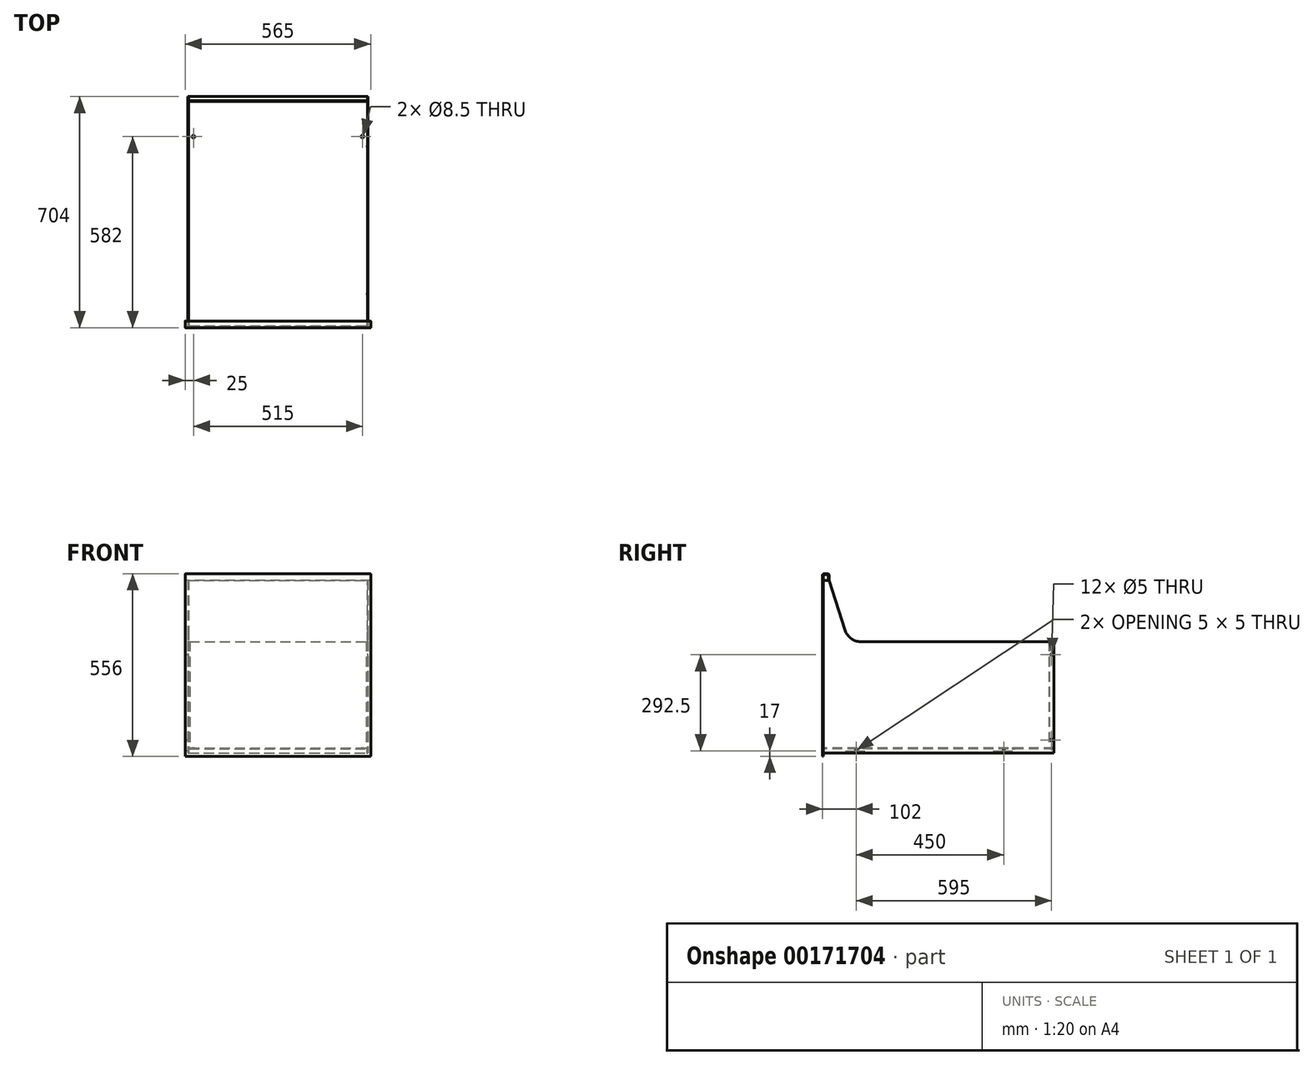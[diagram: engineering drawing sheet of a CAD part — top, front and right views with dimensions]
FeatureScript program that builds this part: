
annotation { "Feature Type Name" : "Feature", "Feature Type Description" : "" }
export const myFeature = defineFeature(function(context is Context, id is Id, definition is map)
    precondition{}
    {
        {
            var Q0;
            Q0=qCreatedBy(makeId("Top.planeOp"),FACE);
            var sketch = newSketch(context, id + "F0", { "sketchPlane" : qUnion([Q0])});
            skLineSegment(sketch, "E0.top", {"start": v(-270.5, -351) * mm, "end": v(270.5, -351) * mm});
            skLineSegment(sketch, "E0.left", {"start": v(-274.5, 351) * mm, "end": v(-274.5, -347) * mm});
            skLineSegment(sketch, "E0.right", {"start": v(274.5, 351) * mm, "end": v(274.5, -347) * mm});
            skPoint(sketch, "E0.middle", {"position": v(0, 0) * mm});
            skLineSegment(sketch, "E1", {"start": v(-274.5, 351) * mm, "end": v(274.5, 351) * mm, "construction": true});
            skLineSegment(sketch, "E2", {"start": v(-274.5, 351) * mm, "end": v(-272.5, 351) * mm});
            skLineSegment(sketch, "E3", {"start": v(-272.5, 351) * mm, "end": v(-272.5, -349) * mm});
            skLineSegment(sketch, "E4", {"start": v(-272.5, -349) * mm, "end": v(272.5, -349) * mm});
            skLineSegment(sketch, "E5", {"start": v(272.5, -349) * mm, "end": v(272.5, 351) * mm});
            skPoint(sketch, "E6.visualSharp", {"position": v(-274.5, -351) * mm});
            skArc(sketch, "E6.filletArc", {"start": v(-274.5, -347) * mm, "mid": v(-273.33, -349.83) * mm, "end": v(-270.5, -351) * mm});
            skPoint(sketch, "E7.visualSharp", {"position": v(274.5, -351) * mm});
            skArc(sketch, "E7.filletArc", {"start": v(270.5, -351) * mm, "mid": v(273.33, -349.83) * mm, "end": v(274.5, -347) * mm});
            skLineSegment(sketch, "E8", {"start": v(272.5, 351) * mm, "end": v(274.5, 351) * mm});
            skSolve(sketch);
        }
        {
            var Q0;
            Q0=makeQuery(id+"F0.imprint","IMPRINT",FACE,{"disambiguationData":[TD([[makeQuery(id+"F0.imprint","IMPRINT",EDGE,{"derivedFrom":sQuery(id+"F0.wireOp",EDGE,"E0.top")}),1.0]])]});
            extrude(context, id + "F1", {"entities" : qUnion([Q0]), "depth" : 526 * mm});
        }
        {
            var Q0;
            Q0=makeQuery(id+"F1.opExtrude","SWEPT_FACE",FACE,{"disambiguationData":[OSD([sQuery(id+"F0.wireOp",EDGE,"E4")])]});
            var sketch = newSketch(context, id + "F2", { "sketchPlane" : qUnion([Q0])});
            skLineSegment(sketch, "E9", {"start": v(-272.5, 0) * mm, "end": v(-272.5, 11) * mm});
            skLineSegment(sketch, "E10", {"start": v(-268.5, 15) * mm, "end": v(268.5, 15) * mm});
            skLineSegment(sketch, "E11", {"start": v(272.5, 11) * mm, "end": v(272.5, 0) * mm});
            skLineSegment(sketch, "E12", {"start": v(272.5, 0) * mm, "end": v(270.5, 0) * mm});
            skLineSegment(sketch, "E13", {"start": v(270.5, 0) * mm, "end": v(270.5, 13) * mm});
            skLineSegment(sketch, "E14", {"start": v(270.5, 13) * mm, "end": v(-270.5, 13) * mm});
            skLineSegment(sketch, "E15", {"start": v(-270.5, 13) * mm, "end": v(-270.5, 0) * mm});
            skLineSegment(sketch, "E16", {"start": v(-270.5, 0) * mm, "end": v(-272.5, 0) * mm});
            skPoint(sketch, "E17.visualSharp", {"position": v(272.5, 15) * mm});
            skArc(sketch, "E17.filletArc", {"start": v(272.5, 11) * mm, "mid": v(271.33, 13.83) * mm, "end": v(268.5, 15) * mm});
            skPoint(sketch, "E18.visualSharp", {"position": v(-272.5, 15) * mm});
            skArc(sketch, "E18.filletArc", {"start": v(-268.5, 15) * mm, "mid": v(-271.33, 13.83) * mm, "end": v(-272.5, 11) * mm});
            skSolve(sketch);
        }
        {
            var Q0;
            Q0=makeQuery(id+"F2.imprint","IMPRINT",FACE,{"disambiguationData":[TD([[makeQuery(id+"F2.imprint","IMPRINT",EDGE,{"derivedFrom":sQuery(id+"F2.wireOp",EDGE,"E9")}),1.0]])]});
            var Q1;
            Q1=makeQuery(id+"F1.opExtrude","SWEPT_FACE",FACE,{"disambiguationData":[OSD([sQuery(id+"F0.wireOp",EDGE,"E2")])]});
            extrude(context, id + "F3", {"entities" : qUnion([Q0]), "endBound" : BoundingType.UP_TO_SURFACE, "endBoundEntityFace" : qUnion([Q1]), "depth" : 25 * mm});
        }
        {
            var Q0;
            Q0=makeQuery(id+"F3.opExtrude","SWEPT_FACE",FACE,{"disambiguationData":[OSD([sQuery(id+"F2.wireOp",EDGE,"E10")])]});
            var sketch = newSketch(context, id + "F4", { "sketchPlane" : qUnion([Q0])});
            skLineSegment(sketch, "E19.0", {"start": v(272.5, -349) * mm, "end": v(272.5, 351) * mm});
            skLineSegment(sketch, "E20.0", {"start": v(-272.5, 351) * mm, "end": v(-272.5, -349) * mm});
            skLineSegment(sketch, "E21", {"start": v(-272.5, 351) * mm, "end": v(-272.5, 340) * mm});
            skLineSegment(sketch, "E22", {"start": v(-268.5, 336) * mm, "end": v(268.5, 336) * mm});
            skLineSegment(sketch, "E23", {"start": v(272.5, 340) * mm, "end": v(272.5, 351) * mm});
            skLineSegment(sketch, "E24", {"start": v(272.5, 351) * mm, "end": v(270.5, 351) * mm});
            skLineSegment(sketch, "E25", {"start": v(270.5, 351) * mm, "end": v(270.5, 338) * mm});
            skLineSegment(sketch, "E26", {"start": v(270.5, 338) * mm, "end": v(-270.5, 338) * mm});
            skLineSegment(sketch, "E27", {"start": v(-270.5, 338) * mm, "end": v(-270.5, 351) * mm});
            skLineSegment(sketch, "E28", {"start": v(-270.5, 351) * mm, "end": v(-272.5, 351) * mm});
            skPoint(sketch, "E29.visualSharp", {"position": v(272.5, 336) * mm});
            skArc(sketch, "E29.filletArc", {"start": v(268.5, 336) * mm, "mid": v(271.33, 337.17) * mm, "end": v(272.5, 340) * mm});
            skPoint(sketch, "E30.visualSharp", {"position": v(-272.5, 336) * mm});
            skArc(sketch, "E30.filletArc", {"start": v(-272.5, 340) * mm, "mid": v(-271.33, 337.17) * mm, "end": v(-268.5, 336) * mm});
            skSolve(sketch);
        }
        {
            var Q0;
            {var subQ0=sQuery(id+"F4.wireOp",EDGE,"E22");Q0=makeQuery(id+"F4.imprint","IMPRINT",FACE,{"disambiguationData":[TD([[makeQuery(id+"F4.imprint","IMPRINT",EDGE,{"derivedFrom":subQ0}),1.0]])]});}
            var Q1;
            Q1=makeQuery(id+"F4.imprint","IMPRINT",FACE,{"disambiguationData":[TD([[makeQuery(id+"F4.imprint","IMPRINT",EDGE,{"derivedFrom":sQuery(id+"F4.wireOp",EDGE,"E21")}),1.0]])]});
            var Q2;
            Q2=makeQuery(id+"F4.imprint","IMPRINT",FACE,{"disambiguationData":[TD([[makeQuery(id+"F4.imprint","IMPRINT",EDGE,{"derivedFrom":sQuery(id+"F4.wireOp",EDGE,"E23")}),1.0]])]});
            extrude(context, id + "F5", {"entities" : qUnion([Q0, Q1, Q2]), "depth" : 324.5 * mm});
        }
        {
            var Q0;
            Q0=makeQuery(id+"F1.opExtrude","SWEPT_FACE",FACE,{"disambiguationData":[OSD([sQuery(id+"F0.wireOp",EDGE,"E0.right")])]});
            var sketch = newSketch(context, id + "F6", { "sketchPlane" : qUnion([Q0])});
            skLineSegment(sketch, "E31.0", {"start": v(-351, 526) * mm, "end": v(-351, 0) * mm});
            skLineSegment(sketch, "E32", {"start": v(-374.1, 7) * mm, "end": v(407.57, 7) * mm, "construction": true});
            skLineSegment(sketch, "E33", {"start": v(344, -59.87) * mm, "end": v(344, 378.9) * mm, "construction": true});
            skPoint(sketch, "E34", {"position": v(-251, 7) * mm});
            skPoint(sketch, "E35", {"position": v(199, 7) * mm});
            skPoint(sketch, "E36", {"position": v(344, 299.5) * mm});
            skPoint(sketch, "E37", {"position": v(344, 40) * mm});
            skLineSegment(sketch, "E38.0", {"start": v(340, 339.5) * mm, "end": v(351, 339.5) * mm});
            skLineSegment(sketch, "E39", {"start": v(-351, 526) * mm, "end": v(-333, 526) * mm});
            skLineSegment(sketch, "E40", {"start": v(-333, 526) * mm, "end": v(-284.64, 374.31) * mm});
            skLineSegment(sketch, "E41", {"start": v(-237, 339.5) * mm, "end": v(340, 339.5) * mm});
            skPoint(sketch, "E42.visualSharp", {"position": v(-273.54, 339.5) * mm});
            skArc(sketch, "E42.filletArc", {"start": v(-284.64, 374.31) * mm, "mid": v(-266.5, 349.13) * mm, "end": v(-237, 339.5) * mm});
            skSolve(sketch);
        }
        {
            var Q0;
            Q0=sQuery(id+"F6.wireOp",VERTEX,"E37");
            var Q1;
            Q1=sQuery(id+"F6.wireOp",VERTEX,"E35");
            var Q2;
            Q2=sQuery(id+"F6.wireOp",VERTEX,"E36");
            var Q3;
            Q3=sQuery(id+"F6.wireOp",VERTEX,"E34");
            var Q4;
            Q4=makeQuery(id+"F1.opExtrude","SWEPT_BODY",BODY,{"disambiguationData":[OSD([sQuery(id+"F0.wireOp",EDGE,"E0.top"),sQuery(id+"F0.wireOp",EDGE,"E0.left"),sQuery(id+"F0.wireOp",EDGE,"E0.right"),sQuery(id+"F0.wireOp",EDGE,"E2"),sQuery(id+"F0.wireOp",EDGE,"E3"),sQuery(id+"F0.wireOp",EDGE,"E4"),sQuery(id+"F0.wireOp",EDGE,"E5"),sQuery(id+"F0.wireOp",EDGE,"E6.filletArc"),sQuery(id+"F0.wireOp",EDGE,"E7.filletArc"),sQuery(id+"F0.wireOp",EDGE,"E8")])]});
            var Q5;
            Q5=makeQuery(id+"F3.opExtrude","SWEPT_BODY",BODY,{"disambiguationData":[OSD([sQuery(id+"F2.wireOp",EDGE,"E9"),sQuery(id+"F2.wireOp",EDGE,"E10"),sQuery(id+"F2.wireOp",EDGE,"E11"),sQuery(id+"F2.wireOp",EDGE,"E12"),sQuery(id+"F2.wireOp",EDGE,"E13"),sQuery(id+"F2.wireOp",EDGE,"E14"),sQuery(id+"F2.wireOp",EDGE,"E15"),sQuery(id+"F2.wireOp",EDGE,"E16"),sQuery(id+"F2.wireOp",EDGE,"E17.filletArc"),sQuery(id+"F2.wireOp",EDGE,"E18.filletArc")])]});
            var Q6;
            Q6=makeQuery(id+"F5.opExtrude","SWEPT_BODY",BODY,{"disambiguationData":[OSD([sQuery(id+"F4.wireOp",EDGE,"E21"),sQuery(id+"F4.wireOp",EDGE,"E22"),sQuery(id+"F4.wireOp",EDGE,"E23"),sQuery(id+"F4.wireOp",EDGE,"E24"),sQuery(id+"F4.wireOp",EDGE,"E25"),sQuery(id+"F4.wireOp",EDGE,"E26"),sQuery(id+"F4.wireOp",EDGE,"E27"),sQuery(id+"F4.wireOp",EDGE,"E28"),sQuery(id+"F4.wireOp",EDGE,"E29.filletArc"),sQuery(id+"F4.wireOp",EDGE,"E30.filletArc")])]});
            hole(context, id + "F7", {"style" : HoleStyle.C_SINK, "endStyle" : HoleEndStyle.BLIND, "holeDiameter" : 5 * mm, "cSinkDiameter" : 5 * mm, "cSinkAngle" : 90 * degree, "holeDepth" : 2000 * mm, "startFromSketch" : true, "locations" : qUnion([Q0, Q1, Q2, Q3]), "scope" : qUnion([Q4, Q5, Q6])});
        }
        {
            var Q0;
            Q0=qCreatedBy(makeId("Right.planeOp"),FACE);
            var sketch = newSketch(context, id + "F8", { "sketchPlane" : qUnion([Q0])});
            skPoint(sketch, "E43.0", {"position": v(-351, 526) * mm});
            skPoint(sketch, "E44.0", {"position": v(-351, 0) * mm});
            skLineSegment(sketch, "E45.0", {"start": v(351, 526) * mm, "end": v(-347, 526) * mm});
            skLineSegment(sketch, "E46", {"start": v(-351, 526) * mm, "end": v(-351, 544) * mm});
            skLineSegment(sketch, "E47", {"start": v(-351, 544) * mm, "end": v(-335, 544) * mm});
            skLineSegment(sketch, "E48", {"start": v(-335, 544) * mm, "end": v(-335, 526) * mm});
            skLineSegment(sketch, "E49", {"start": v(-335, 526) * mm, "end": v(-333, 526) * mm});
            skLineSegment(sketch, "E50", {"start": v(-333, 526) * mm, "end": v(-333, 542) * mm});
            skLineSegment(sketch, "E51", {"start": v(-337, 546) * mm, "end": v(-349, 546) * mm});
            skLineSegment(sketch, "E52", {"start": v(-353, 542) * mm, "end": v(-353, 526) * mm});
            skLineSegment(sketch, "E53", {"start": v(-353, 526) * mm, "end": v(-351, 526) * mm});
            skPoint(sketch, "E54.visualSharp", {"position": v(-353, 546) * mm});
            skArc(sketch, "E54.filletArc", {"start": v(-349, 546) * mm, "mid": v(-351.83, 544.83) * mm, "end": v(-353, 542) * mm});
            skPoint(sketch, "E55.visualSharp", {"position": v(-333, 546) * mm});
            skArc(sketch, "E55.filletArc", {"start": v(-333, 542) * mm, "mid": v(-334.17, 544.83) * mm, "end": v(-337, 546) * mm});
            skLineSegment(sketch, "E56", {"start": v(-351, 0) * mm, "end": v(-351, -10) * mm});
            skLineSegment(sketch, "E57", {"start": v(-351, -10) * mm, "end": v(-353, -10) * mm});
            skLineSegment(sketch, "E58", {"start": v(-353, -10) * mm, "end": v(-353, 0) * mm});
            skLineSegment(sketch, "E59", {"start": v(-353, 0) * mm, "end": v(-351, 0) * mm});
            skLineSegment(sketch, "E60", {"start": v(-351, 0) * mm, "end": v(-351, 526) * mm});
            skLineSegment(sketch, "E61", {"start": v(-353, 526) * mm, "end": v(-353, 0) * mm});
            skSolve(sketch);
        }
        {
            var Q0;
            Q0=makeQuery(id+"F8.imprint","IMPRINT",FACE,{"disambiguationData":[TD([[makeQuery(id+"F8.imprint","IMPRINT",EDGE,{"derivedFrom":sQuery(id+"F8.wireOp",EDGE,"E56")}),-1.0]])]});
            var Q1;
            Q1=makeQuery(id+"F8.imprint","IMPRINT",FACE,{"disambiguationData":[TD([[makeQuery(id+"F8.imprint","IMPRINT",EDGE,{"derivedFrom":sQuery(id+"F8.wireOp",EDGE,"E53")}),-1.0]])]});
            var Q2;
            Q2=makeQuery(id+"F8.imprint","IMPRINT",FACE,{"disambiguationData":[TD([[makeQuery(id+"F8.imprint","IMPRINT",EDGE,{"derivedFrom":sQuery(id+"F8.wireOp",EDGE,"E46")}),1.0]])]});
            extrude(context, id + "F9", {"entities" : qUnion([Q0, Q1, Q2]), "endBound" : BoundingType.SYMMETRIC, "depth" : 565 * mm});
        }
        {
            var Q0;
            {var subQ5=sQuery(id+"F6.wireOp",EDGE,"E38.0");Q0=makeQuery(id+"F6.imprint","IMPRINT",FACE,{"disambiguationData":[TD([[makeQuery(id+"F6.imprint","IMPRINT",EDGE,{"derivedFrom":subQ5}),1.0]])]});}
            extrude(context, id + "F10", {"entities" : qUnion([Q0]), "operationType" : NewBodyOperationType.REMOVE, "oppositeDirection" : true, "depth" : 1000 * mm});
        }
        {
            var Q0;
            Q0=makeQuery(id+"F3.opExtrude","SWEPT_FACE",FACE,{"disambiguationData":[OSD([sQuery(id+"F2.wireOp",EDGE,"E14")])]});
            var sketch = newSketch(context, id + "F11", { "sketchPlane" : qUnion([Q0])});
            skLineSegment(sketch, "E62.0", {"start": v(-272.5, 349) * mm, "end": v(272.5, 349) * mm});
            skLineSegment(sketch, "E63.0", {"start": v(-272.5, -351) * mm, "end": v(-272.5, 349) * mm});
            skLineSegment(sketch, "E64.0", {"start": v(272.5, 349) * mm, "end": v(272.5, -351) * mm});
            skLineSegment(sketch, "E65", {"start": v(345.66, -229) * mm, "end": v(-405.33, -229) * mm, "construction": true});
            skPoint(sketch, "E66", {"position": v(257.5, -229) * mm});
            skPoint(sketch, "E67", {"position": v(-257.5, -229) * mm});
            skSolve(sketch);
        }
        {
            var Q0;
            Q0=sQuery(id+"F11.wireOp",VERTEX,"E67");
            var Q1;
            Q1=sQuery(id+"F11.wireOp",VERTEX,"E66");
            var Q2;
            Q2=makeQuery(id+"F3.opExtrude","SWEPT_BODY",BODY,{"disambiguationData":[OSD([sQuery(id+"F2.wireOp",EDGE,"E9"),sQuery(id+"F2.wireOp",EDGE,"E10"),sQuery(id+"F2.wireOp",EDGE,"E11"),sQuery(id+"F2.wireOp",EDGE,"E12"),sQuery(id+"F2.wireOp",EDGE,"E13"),sQuery(id+"F2.wireOp",EDGE,"E14"),sQuery(id+"F2.wireOp",EDGE,"E15"),sQuery(id+"F2.wireOp",EDGE,"E16"),sQuery(id+"F2.wireOp",EDGE,"E17.filletArc"),sQuery(id+"F2.wireOp",EDGE,"E18.filletArc")])]});
            hole(context, id + "F12", {"style" : HoleStyle.C_SINK, "endStyle" : HoleEndStyle.BLIND, "holeDiameter" : 8.5 * mm, "cSinkDiameter" : 8.5 * mm, "cSinkAngle" : 90 * degree, "holeDepth" : 20 * mm, "startFromSketch" : true, "locations" : qUnion([Q0, Q1]), "scope" : qUnion([Q2])});
        }
    });
